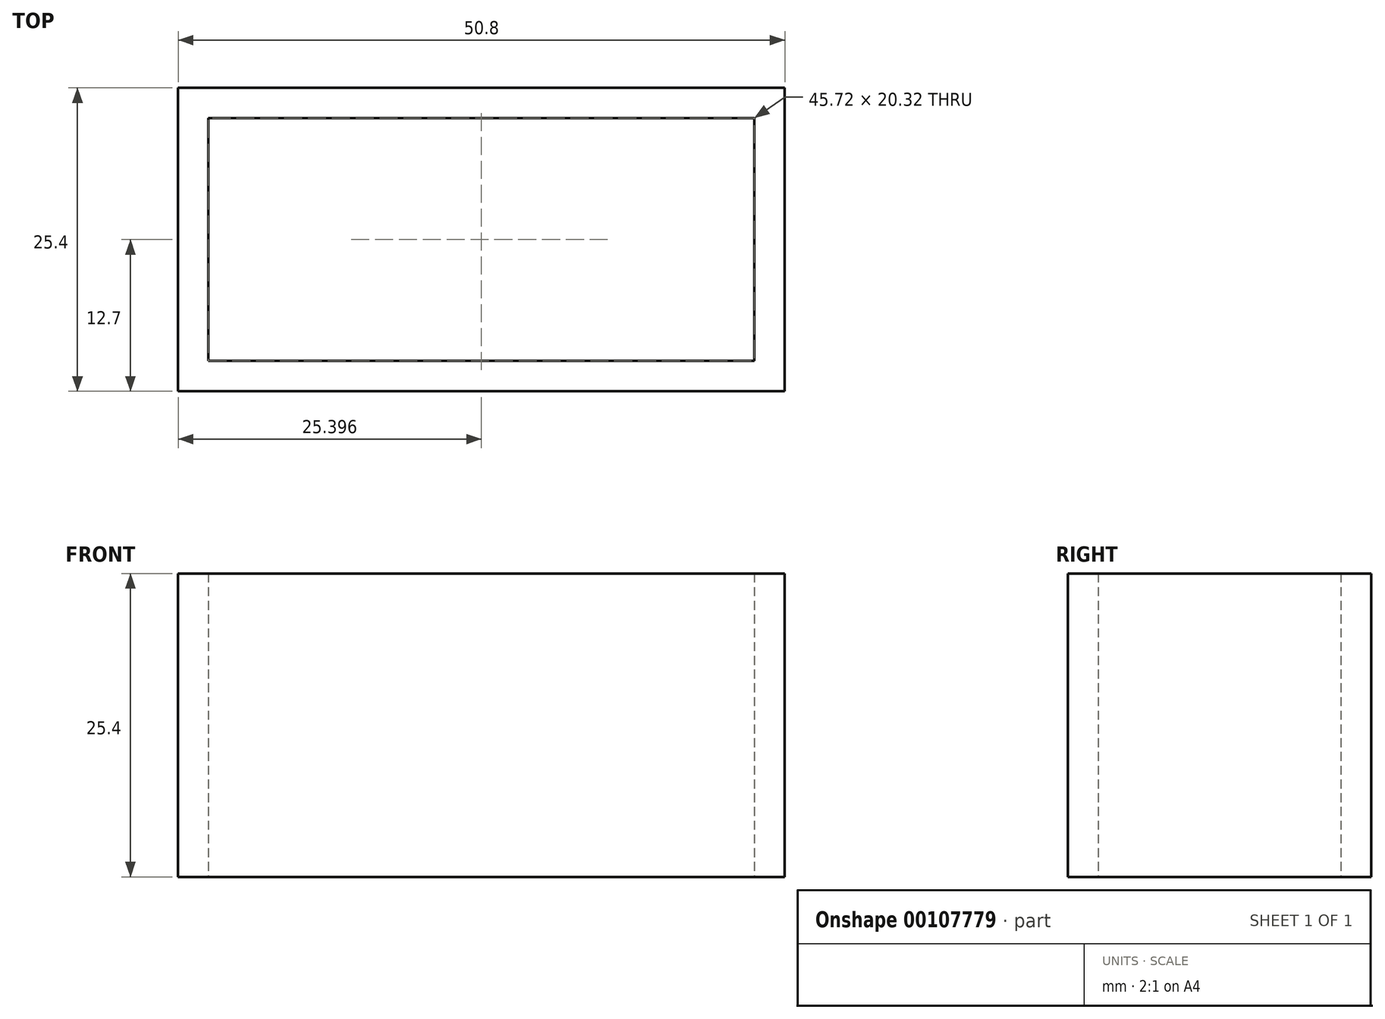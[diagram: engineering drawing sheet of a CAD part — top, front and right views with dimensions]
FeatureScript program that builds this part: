
annotation { "Feature Type Name" : "Feature", "Feature Type Description" : "" }
export const myFeature = defineFeature(function(context is Context, id is Id, definition is map)
    precondition{}
    {
        {
            var Q0;
            Q0=qCreatedBy(makeId("Top.planeOp"),FACE);
            var sketch = newSketch(context, id + "F0", { "sketchPlane" : qUnion([Q0])});
            skLineSegment(sketch, "E0.bottom", {"start": v(-22.7, 2.54) * mm, "end": v(28.1, 2.54) * mm});
            skLineSegment(sketch, "E0.top", {"start": v(-22.7, -22.86) * mm, "end": v(28.1, -22.86) * mm});
            skLineSegment(sketch, "E0.left", {"start": v(-22.7, 2.54) * mm, "end": v(-22.7, -22.86) * mm});
            skLineSegment(sketch, "E0.right", {"start": v(28.1, 2.54) * mm, "end": v(28.1, -22.86) * mm});
            skLineSegment(sketch, "E1", {"start": v(-22.7, 2.54) * mm, "end": v(28.1, -22.86) * mm, "construction": true});
            skLineSegment(sketch, "E2.bottom", {"start": v(-20.16, 0) * mm, "end": v(25.56, 0) * mm});
            skLineSegment(sketch, "E2.top", {"start": v(-20.16, -20.32) * mm, "end": v(25.56, -20.32) * mm});
            skLineSegment(sketch, "E2.left", {"start": v(-20.16, 0) * mm, "end": v(-20.16, -20.32) * mm});
            skLineSegment(sketch, "E2.right", {"start": v(25.56, 0) * mm, "end": v(25.56, -20.32) * mm});
            skPoint(sketch, "E2.middle", {"position": v(2.7, -10.16) * mm});
            skSolve(sketch);
        }
        {
            var Q0;
            Q0 = qSketchRegion(id + "F0", true);
            extrude(context, id + "F1", {"entities" : qUnion([Q0]), "depth" : 25.4 * mm});
        }
    });
